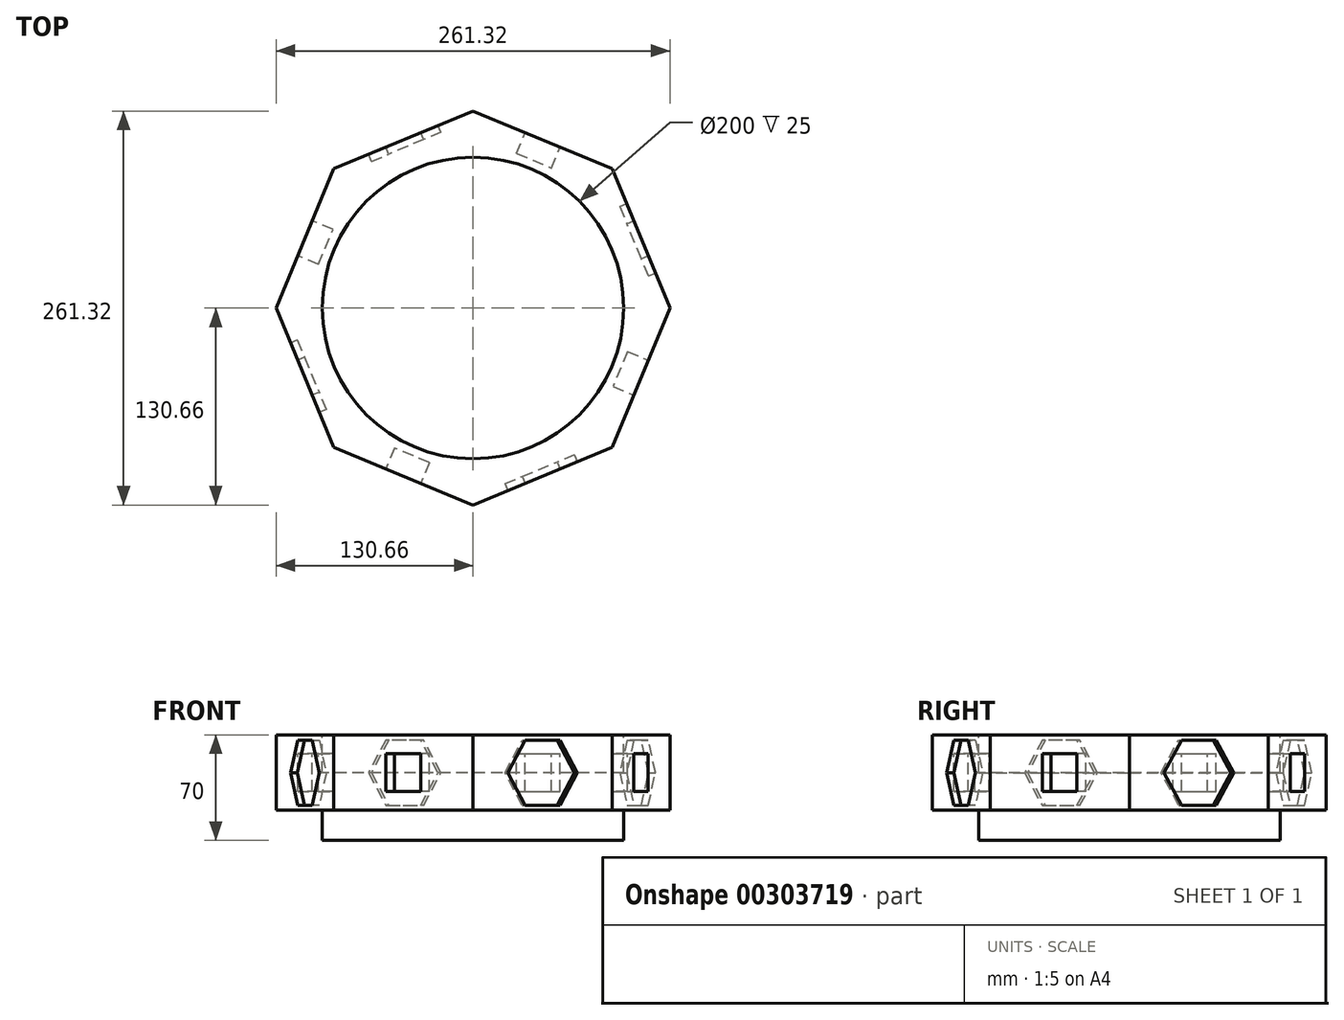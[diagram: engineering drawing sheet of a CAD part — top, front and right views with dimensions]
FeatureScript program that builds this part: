
annotation { "Feature Type Name" : "Feature", "Feature Type Description" : "" }
export const myFeature = defineFeature(function(context is Context, id is Id, definition is map)
    precondition{}
    {
        {
            var Q0;
            Q0=qCreatedBy(makeId("Top.planeOp"),FACE);
            var sketch = newSketch(context, id + "F0", { "sketchPlane" : qUnion([Q0])});
            skCircle(sketch, "E0.cCircle", {"center": v(0, 0) * mm, "radius": 130.66 * mm, "construction": true});
            skLineSegment(sketch, "E0.0", {"start": v(0, -130.66) * mm, "end": v(-92.39, -92.39) * mm});
            skLineSegment(sketch, "E0.1", {"start": v(-92.39, -92.39) * mm, "end": v(-130.66, 0) * mm});
            skLineSegment(sketch, "E0.2", {"start": v(-130.66, 0) * mm, "end": v(-92.39, 92.39) * mm});
            skLineSegment(sketch, "E0.3", {"start": v(-92.39, 92.39) * mm, "end": v(0, 130.66) * mm});
            skLineSegment(sketch, "E0.4", {"start": v(0, 130.66) * mm, "end": v(92.39, 92.39) * mm});
            skLineSegment(sketch, "E0.5", {"start": v(92.39, 92.39) * mm, "end": v(130.66, 0) * mm});
            skLineSegment(sketch, "E0.6", {"start": v(130.66, 0) * mm, "end": v(92.39, -92.39) * mm});
            skLineSegment(sketch, "E0.7", {"start": v(92.39, -92.39) * mm, "end": v(0, -130.66) * mm});
            skSolve(sketch);
        }
        {
            var Q0;
            Q0=makeQuery(id+"F0.imprint","IMPRINT",FACE,{"disambiguationData":[TD([[makeQuery(id+"F0.imprint","IMPRINT",EDGE,{"derivedFrom":sQuery(id+"F0.wireOp",EDGE,"E0.0")}),-1.0]])]});
            extrude(context, id + "F1", {"entities" : qUnion([Q0]), "depth" : 50 * mm});
        }
        {
            var Q0;
            Q0=makeQuery(id+"F1.opExtrude","SWEPT_FACE",FACE,{"disambiguationData":[OSD([sQuery(id+"F0.wireOp",EDGE,"E0.0")])]});
            var sketch = newSketch(context, id + "F2", { "sketchPlane" : qUnion([Q0])});
            skLineSegment(sketch, "E1.bottom", {"start": v(12.5, 12.5) * mm, "end": v(-12.5, 12.5) * mm});
            skLineSegment(sketch, "E1.top", {"start": v(12.5, 37.5) * mm, "end": v(-12.5, 37.5) * mm});
            skLineSegment(sketch, "E1.left", {"start": v(12.5, 12.5) * mm, "end": v(12.5, 37.5) * mm});
            skLineSegment(sketch, "E1.right", {"start": v(-12.5, 12.5) * mm, "end": v(-12.5, 37.5) * mm});
            skPoint(sketch, "E1.middle", {"position": v(0, 25) * mm});
            skPoint(sketch, "E1.middle.positionSnap0", {"position": v(-50, 25) * mm});
            skPoint(sketch, "E1.centerSnap0", {"position": v(-50, 25) * mm});
            skSolve(sketch);
        }
        {
            var Q0;
            Q0=makeQuery(id+"F2.imprint","IMPRINT",FACE,{"disambiguationData":[TD([[makeQuery(id+"F2.imprint","IMPRINT",EDGE,{"derivedFrom":sQuery(id+"F2.wireOp",EDGE,"E1.bottom")}),-1.0]])]});
            extrude(context, id + "F3", {"entities" : qUnion([Q0]), "operationType" : NewBodyOperationType.REMOVE, "oppositeDirection" : true, "depth" : 15 * mm});
        }
        {
            var Q0;
            Q0=makeQuery(id+"F1.opExtrude","SWEPT_FACE",FACE,{"disambiguationData":[OSD([sQuery(id+"F0.wireOp",EDGE,"E0.2")])]});
            var sketch = newSketch(context, id + "F4", { "sketchPlane" : qUnion([Q0])});
            skLineSegment(sketch, "E2.bottom", {"start": v(12.5, 12.5) * mm, "end": v(-12.5, 12.5) * mm});
            skLineSegment(sketch, "E2.top", {"start": v(12.5, 37.5) * mm, "end": v(-12.5, 37.5) * mm});
            skLineSegment(sketch, "E2.left", {"start": v(12.5, 12.5) * mm, "end": v(12.5, 37.5) * mm});
            skLineSegment(sketch, "E2.right", {"start": v(-12.5, 12.5) * mm, "end": v(-12.5, 37.5) * mm});
            skPoint(sketch, "E2.middle", {"position": v(0, 25) * mm});
            skPoint(sketch, "E2.middle.positionSnap0", {"position": v(-50, 25) * mm});
            skPoint(sketch, "E2.centerSnap0", {"position": v(-50, 25) * mm});
            skSolve(sketch);
        }
        {
            var Q0;
            Q0=makeQuery(id+"F4.imprint","IMPRINT",FACE,{"disambiguationData":[TD([[makeQuery(id+"F4.imprint","IMPRINT",EDGE,{"derivedFrom":sQuery(id+"F4.wireOp",EDGE,"E2.bottom")}),-1.0]])]});
            extrude(context, id + "F5", {"entities" : qUnion([Q0]), "operationType" : NewBodyOperationType.REMOVE, "oppositeDirection" : true, "depth" : 15 * mm});
        }
        {
            var Q0;
            Q0=makeQuery(id+"F1.opExtrude","SWEPT_FACE",FACE,{"disambiguationData":[OSD([sQuery(id+"F0.wireOp",EDGE,"E0.4")])]});
            var sketch = newSketch(context, id + "F6", { "sketchPlane" : qUnion([Q0])});
            skLineSegment(sketch, "E3.bottom", {"start": v(12.5, 12.5) * mm, "end": v(-12.5, 12.5) * mm});
            skLineSegment(sketch, "E3.top", {"start": v(12.5, 37.5) * mm, "end": v(-12.5, 37.5) * mm});
            skLineSegment(sketch, "E3.left", {"start": v(12.5, 12.5) * mm, "end": v(12.5, 37.5) * mm});
            skLineSegment(sketch, "E3.right", {"start": v(-12.5, 12.5) * mm, "end": v(-12.5, 37.5) * mm});
            skPoint(sketch, "E3.middle", {"position": v(0, 25) * mm});
            skPoint(sketch, "E3.middle.positionSnap0", {"position": v(-50, 25) * mm});
            skPoint(sketch, "E3.centerSnap0", {"position": v(-50, 25) * mm});
            skSolve(sketch);
        }
        {
            var Q0;
            Q0=makeQuery(id+"F6.imprint","IMPRINT",FACE,{"disambiguationData":[TD([[makeQuery(id+"F6.imprint","IMPRINT",EDGE,{"derivedFrom":sQuery(id+"F6.wireOp",EDGE,"E3.bottom")}),-1.0]])]});
            extrude(context, id + "F7", {"entities" : qUnion([Q0]), "operationType" : NewBodyOperationType.REMOVE, "oppositeDirection" : true, "depth" : 15 * mm});
        }
        {
            var Q0;
            Q0=makeQuery(id+"F1.opExtrude","SWEPT_FACE",FACE,{"disambiguationData":[OSD([sQuery(id+"F0.wireOp",EDGE,"E0.6")])]});
            var sketch = newSketch(context, id + "F8", { "sketchPlane" : qUnion([Q0])});
            skLineSegment(sketch, "E4.bottom", {"start": v(12.5, 12.5) * mm, "end": v(-12.5, 12.5) * mm});
            skLineSegment(sketch, "E4.top", {"start": v(12.5, 37.5) * mm, "end": v(-12.5, 37.5) * mm});
            skLineSegment(sketch, "E4.left", {"start": v(12.5, 12.5) * mm, "end": v(12.5, 37.5) * mm});
            skLineSegment(sketch, "E4.right", {"start": v(-12.5, 12.5) * mm, "end": v(-12.5, 37.5) * mm});
            skPoint(sketch, "E4.middle", {"position": v(0, 25) * mm});
            skPoint(sketch, "E4.middle.positionSnap0", {"position": v(-50, 25) * mm});
            skPoint(sketch, "E4.centerSnap0", {"position": v(-50, 25) * mm});
            skSolve(sketch);
        }
        {
            var Q0;
            Q0=makeQuery(id+"F8.imprint","IMPRINT",FACE,{"disambiguationData":[TD([[makeQuery(id+"F8.imprint","IMPRINT",EDGE,{"derivedFrom":sQuery(id+"F8.wireOp",EDGE,"E4.bottom")}),-1.0]])]});
            extrude(context, id + "F9", {"entities" : qUnion([Q0]), "operationType" : NewBodyOperationType.REMOVE, "oppositeDirection" : true, "depth" : 15 * mm});
        }
        {
            var Q0;
            Q0=makeQuery(id+"F1.opExtrude","SWEPT_FACE",FACE,{"disambiguationData":[OSD([sQuery(id+"F0.wireOp",EDGE,"E0.7")])]});
            var sketch = newSketch(context, id + "F10", { "sketchPlane" : qUnion([Q0])});
            skCircle(sketch, "E5.cCircle", {"center": v(0, 25) * mm, "radius": 21.65 * mm, "construction": true});
            skPoint(sketch, "E5.cCircle.centerSnap0", {"position": v(-50, 25) * mm});
            skLineSegment(sketch, "E5.0", {"start": v(25, 25) * mm, "end": v(12.5, 3.35) * mm});
            skLineSegment(sketch, "E5.1", {"start": v(12.5, 3.35) * mm, "end": v(-12.5, 3.35) * mm});
            skLineSegment(sketch, "E5.2", {"start": v(-12.5, 3.35) * mm, "end": v(-25, 25) * mm});
            skLineSegment(sketch, "E5.3", {"start": v(-25, 25) * mm, "end": v(-12.5, 46.65) * mm});
            skLineSegment(sketch, "E5.4", {"start": v(-12.5, 46.65) * mm, "end": v(12.5, 46.65) * mm});
            skLineSegment(sketch, "E5.5", {"start": v(12.5, 46.65) * mm, "end": v(25, 25) * mm});
            skPoint(sketch, "E5.0.midPoint", {"position": v(18.75, 14.17) * mm});
            skSolve(sketch);
        }
        {
            var Q0;
            Q0=makeQuery(id+"F10.imprint","IMPRINT",FACE,{"disambiguationData":[TD([[makeQuery(id+"F10.imprint","IMPRINT",EDGE,{"derivedFrom":sQuery(id+"F10.wireOp",EDGE,"E5.0")}),-1.0]])]});
            extrude(context, id + "F11", {"entities" : qUnion([Q0]), "operationType" : NewBodyOperationType.REMOVE, "oppositeDirection" : true, "depth" : 5 * mm});
        }
        {
            var Q0;
            Q0=makeQuery(id+"F1.opExtrude","SWEPT_FACE",FACE,{"disambiguationData":[OSD([sQuery(id+"F0.wireOp",EDGE,"E0.5")])]});
            var sketch = newSketch(context, id + "F12", { "sketchPlane" : qUnion([Q0])});
            skCircle(sketch, "E6.cCircle", {"center": v(0, 25) * mm, "radius": 21.65 * mm, "construction": true});
            skPoint(sketch, "E6.cCircle.centerSnap0", {"position": v(0, 50) * mm});
            skPoint(sketch, "E6.cCircle.centerSnap1", {"position": v(-50, 25) * mm});
            skLineSegment(sketch, "E6.0", {"start": v(25, 25) * mm, "end": v(12.5, 3.35) * mm});
            skLineSegment(sketch, "E6.1", {"start": v(12.5, 3.35) * mm, "end": v(-12.5, 3.35) * mm});
            skLineSegment(sketch, "E6.2", {"start": v(-12.5, 3.35) * mm, "end": v(-25, 25) * mm});
            skLineSegment(sketch, "E6.3", {"start": v(-25, 25) * mm, "end": v(-12.5, 46.65) * mm});
            skLineSegment(sketch, "E6.4", {"start": v(-12.5, 46.65) * mm, "end": v(12.5, 46.65) * mm});
            skLineSegment(sketch, "E6.5", {"start": v(12.5, 46.65) * mm, "end": v(25, 25) * mm});
            skPoint(sketch, "E6.0.midPoint", {"position": v(18.75, 14.17) * mm});
            skSolve(sketch);
        }
        {
            var Q0;
            Q0=makeQuery(id+"F12.imprint","IMPRINT",FACE,{"disambiguationData":[TD([[makeQuery(id+"F12.imprint","IMPRINT",EDGE,{"derivedFrom":sQuery(id+"F12.wireOp",EDGE,"E6.0")}),-1.0]])]});
            extrude(context, id + "F13", {"entities" : qUnion([Q0]), "operationType" : NewBodyOperationType.REMOVE, "oppositeDirection" : true, "depth" : 5 * mm});
        }
        {
            var Q0;
            Q0=makeQuery(id+"F1.opExtrude","SWEPT_FACE",FACE,{"disambiguationData":[OSD([sQuery(id+"F0.wireOp",EDGE,"E0.1")])]});
            var sketch = newSketch(context, id + "F14", { "sketchPlane" : qUnion([Q0])});
            skCircle(sketch, "E7.cCircle", {"center": v(0, 25) * mm, "radius": 21.65 * mm, "construction": true});
            skPoint(sketch, "E7.cCircle.centerSnap0", {"position": v(-50, 25) * mm});
            skLineSegment(sketch, "E7.0", {"start": v(-12.5, 46.65) * mm, "end": v(12.5, 46.65) * mm});
            skLineSegment(sketch, "E7.1", {"start": v(12.5, 46.65) * mm, "end": v(25, 25) * mm});
            skLineSegment(sketch, "E7.2", {"start": v(25, 25) * mm, "end": v(12.5, 3.35) * mm});
            skLineSegment(sketch, "E7.3", {"start": v(12.5, 3.35) * mm, "end": v(-12.5, 3.35) * mm});
            skLineSegment(sketch, "E7.4", {"start": v(-12.5, 3.35) * mm, "end": v(-25, 25) * mm});
            skLineSegment(sketch, "E7.5", {"start": v(-25, 25) * mm, "end": v(-12.5, 46.65) * mm});
            skPoint(sketch, "E7.0.midPoint", {"position": v(0, 46.65) * mm});
            skSolve(sketch);
        }
        {
            var Q0;
            Q0=makeQuery(id+"F14.imprint","IMPRINT",FACE,{"disambiguationData":[TD([[makeQuery(id+"F14.imprint","IMPRINT",EDGE,{"derivedFrom":sQuery(id+"F14.wireOp",EDGE,"E7.0")}),-1.0]])]});
            extrude(context, id + "F15", {"entities" : qUnion([Q0]), "operationType" : NewBodyOperationType.REMOVE, "oppositeDirection" : true, "depth" : 5 * mm});
        }
        {
            var Q0;
            Q0=makeQuery(id+"F1.opExtrude","SWEPT_FACE",FACE,{"disambiguationData":[OSD([sQuery(id+"F0.wireOp",EDGE,"E0.3")])]});
            var sketch = newSketch(context, id + "F16", { "sketchPlane" : qUnion([Q0])});
            skCircle(sketch, "E8.cCircle", {"center": v(0, 25) * mm, "radius": 21.65 * mm, "construction": true});
            skPoint(sketch, "E8.cCircle.centerSnap0", {"position": v(-50, 25) * mm});
            skPoint(sketch, "E8.cCircle.perimeterSnap0", {"position": v(0, 50) * mm});
            skLineSegment(sketch, "E8.0", {"start": v(-12.5, 46.65) * mm, "end": v(12.5, 46.65) * mm});
            skLineSegment(sketch, "E8.1", {"start": v(12.5, 46.65) * mm, "end": v(25, 25) * mm});
            skLineSegment(sketch, "E8.2", {"start": v(25, 25) * mm, "end": v(12.5, 3.35) * mm});
            skLineSegment(sketch, "E8.3", {"start": v(12.5, 3.35) * mm, "end": v(-12.5, 3.35) * mm});
            skLineSegment(sketch, "E8.4", {"start": v(-12.5, 3.35) * mm, "end": v(-25, 25) * mm});
            skLineSegment(sketch, "E8.5", {"start": v(-25, 25) * mm, "end": v(-12.5, 46.65) * mm});
            skPoint(sketch, "E8.0.midPoint", {"position": v(0, 46.65) * mm});
            skPoint(sketch, "E8.0.midPoint.positionSnap0", {"position": v(0, 50) * mm});
            skSolve(sketch);
        }
        {
            var Q0;
            Q0=makeQuery(id+"F16.imprint","IMPRINT",FACE,{"disambiguationData":[TD([[makeQuery(id+"F16.imprint","IMPRINT",EDGE,{"derivedFrom":sQuery(id+"F16.wireOp",EDGE,"E8.0")}),-1.0]])]});
            extrude(context, id + "F17", {"entities" : qUnion([Q0]), "operationType" : NewBodyOperationType.REMOVE, "oppositeDirection" : true, "depth" : 5 * mm});
        }
        {
            var Q0;
            Q0=makeQuery(id+"F1.opExtrude","CAP_FACE",FACE,{"disambiguationData":[OSD([sQuery(id+"F0.wireOp",EDGE,"E0.0"),sQuery(id+"F0.wireOp",EDGE,"E0.1"),sQuery(id+"F0.wireOp",EDGE,"E0.2"),sQuery(id+"F0.wireOp",EDGE,"E0.3"),sQuery(id+"F0.wireOp",EDGE,"E0.4"),sQuery(id+"F0.wireOp",EDGE,"E0.5"),sQuery(id+"F0.wireOp",EDGE,"E0.6"),sQuery(id+"F0.wireOp",EDGE,"E0.7")])],"isStart":false});
            var sketch = newSketch(context, id + "F18", { "sketchPlane" : qUnion([Q0])});
            skCircle(sketch, "E9", {"center": v(0, 0) * mm, "radius": 100 * mm});
            skSolve(sketch);
        }
        {
            var Q0;
            Q0 = qSketchRegion(id + "F18", true);
            extrude(context, id + "F19", {"entities" : qUnion([Q0]), "operationType" : NewBodyOperationType.REMOVE, "oppositeDirection" : true, "depth" : 25 * mm});
        }
        {
            var Q0;
            Q0=makeQuery(id+"F1.opExtrude","CAP_FACE",FACE,{"disambiguationData":[OSD([sQuery(id+"F0.wireOp",EDGE,"E0.0"),sQuery(id+"F0.wireOp",EDGE,"E0.1"),sQuery(id+"F0.wireOp",EDGE,"E0.2"),sQuery(id+"F0.wireOp",EDGE,"E0.3"),sQuery(id+"F0.wireOp",EDGE,"E0.4"),sQuery(id+"F0.wireOp",EDGE,"E0.5"),sQuery(id+"F0.wireOp",EDGE,"E0.6"),sQuery(id+"F0.wireOp",EDGE,"E0.7")])],"isStart":true});
            var sketch = newSketch(context, id + "F20", { "sketchPlane" : qUnion([Q0])});
            skCircle(sketch, "E10", {"center": v(0, 0) * mm, "radius": 100 * mm});
            skSolve(sketch);
        }
        {
            var Q0;
            Q0 = qSketchRegion(id + "F20", true);
            extrude(context, id + "F21", {"entities" : qUnion([Q0]), "operationType" : NewBodyOperationType.ADD, "depth" : 20 * mm});
        }
        {
            var Q0;
            Q0=makeQuery(id+"F1.opExtrude","SWEPT_BODY",BODY,{"disambiguationData":[OSD([sQuery(id+"F0.wireOp",EDGE,"E0.0"),sQuery(id+"F0.wireOp",EDGE,"E0.1"),sQuery(id+"F0.wireOp",EDGE,"E0.2"),sQuery(id+"F0.wireOp",EDGE,"E0.3"),sQuery(id+"F0.wireOp",EDGE,"E0.4"),sQuery(id+"F0.wireOp",EDGE,"E0.5"),sQuery(id+"F0.wireOp",EDGE,"E0.6"),sQuery(id+"F0.wireOp",EDGE,"E0.7")])]});
            transform(context, id + "F22", {"entities" : qUnion([Q0]), "transformType" : TransformType.TRANSLATION_3D, "dx" : 0 * mm, "dy" : 0 * mm, "dz" : 10 * mm, "makeCopy" : false});
        }
    });
